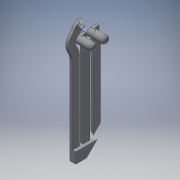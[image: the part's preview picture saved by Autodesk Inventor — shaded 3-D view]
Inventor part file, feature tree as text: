
AUTODESK INVENTOR PART (.ipt)
format: ipt  version: 2016 (Build 200138000, 138)  size: 429,568 bytes
history: native  units: in
note: dims shown in document units (in); Inventor stores cm internally (conversion verified against a paired STEP export)
features: extrude x11, sketch x11, projected_geometry x10, reference x7, fillet x6, plane x5
ambient origin geometry x8: Origin, YZ Plane, XZ Plane, XY Plane, X Axis, Y Axis, Z Axis, Center Point
bodies: Solid1 (feature_tree)
feature tree (50):
  extrude  "Extrusion1"  Depth=0.0079in
  sketch  "Sketch2"  dims[d12=0.052in d13=0.052in d14=0.052in]
  plane  "Work Plane1"
  plane  "Work Plane2"
  extrude  "Extrusion2"  Depth=0.052in
  fillet  "Fillet1"  Radius=0.052in
  extrude  "Extrusion3"  Depth=0.025in
  sketch  "Sketch4"  dims[d18=0.0197in d19=0.0in d20=0.0197in d21=0.0in]
  plane  "Work Plane3"
  extrude  "Extrusion4"  Depth=0.0197in TaperAngle=0.0deg
  extrude  "Extrusion6"  Depth=0.3937in TaperAngle=0.0deg
  fillet  "Fillet5"  Radius=0.0787in
  fillet  "Fillet6"  Radius=0.1969in
  extrude  "Extrusion7"  Depth=0.052in
  fillet  "Fillet8"  Radius=0.125in
  extrude  "Extrusion8"  Depth=0.0039in
  fillet  "Fillet9"  Radius=1.0in
  sketch  "Sketch9"  dims[d42=0.0039in d43=0.0664in]
  plane  "Work Plane4"
  extrude  "Extrusion9"  Depth=0.0664in
  sketch  "Sketch10"  dims[d45=1.0in d46=0.0in d47=0.0079in]
  plane  "Work Plane5"
  extrude  "Extrusion10"  Depth=0.0079in
  extrude  "Extrusion11"  Depth=0.4454in
  extrude  "Extrusion12"  Depth=0.0787in
  fillet  "Fillet10"  Radius=0.1575in
  sketch  "Sketch1"  dims[d9=0.0079in d11=0.0079in]
  reference  "Reference1"
  reference  "Reference2"
  reference  "Reference3"
  reference  "Reference4"
  reference  "Reference5"
  sketch  "Sketch3"  dims[d16=0.025in d17=0.025in]
  projected_geometry  "Projected Loop1"
  projected_geometry  "Projected Loop2"
  projected_geometry  "Projected Loop3"
  projected_geometry  "Projected Loop4"
  projected_geometry  "Projected Loop5"
  projected_geometry  "Projected Loop6"
  sketch  "Sketch6"  dims[d22=0.0197in d23=0.3937in d24=0.0in d25=0.0787in d26=0.1969in d27=0.0in]
  reference  "Reference9"
  sketch  "Sketch7"  dims[d31=0.1181in d36=0.052in d37=0.125in]
  projected_geometry  "Projected Loop7"
  sketch  "Sketch8"  dims[d38=0.0039in d39=0.0039in d40=1.0in d41=0.0in]
  projected_geometry  "Projected Loop8"
  sketch  "Sketch11"  dims[d48=1.0in d49=0.0in d50=0.4454in]
  projected_geometry  "Projected Loop9"
  sketch  "Sketch12"  dims[d51=1.0in d52=0.0in d53=0.0787in d54=0.1575in d55=1.0in d56=0.0in d57=1.0in d58=0.0in d59=0.0197in d60=0.0in d61=0.4454in]
  reference  "Reference10"
  projected_geometry  "Projected Loop10"
